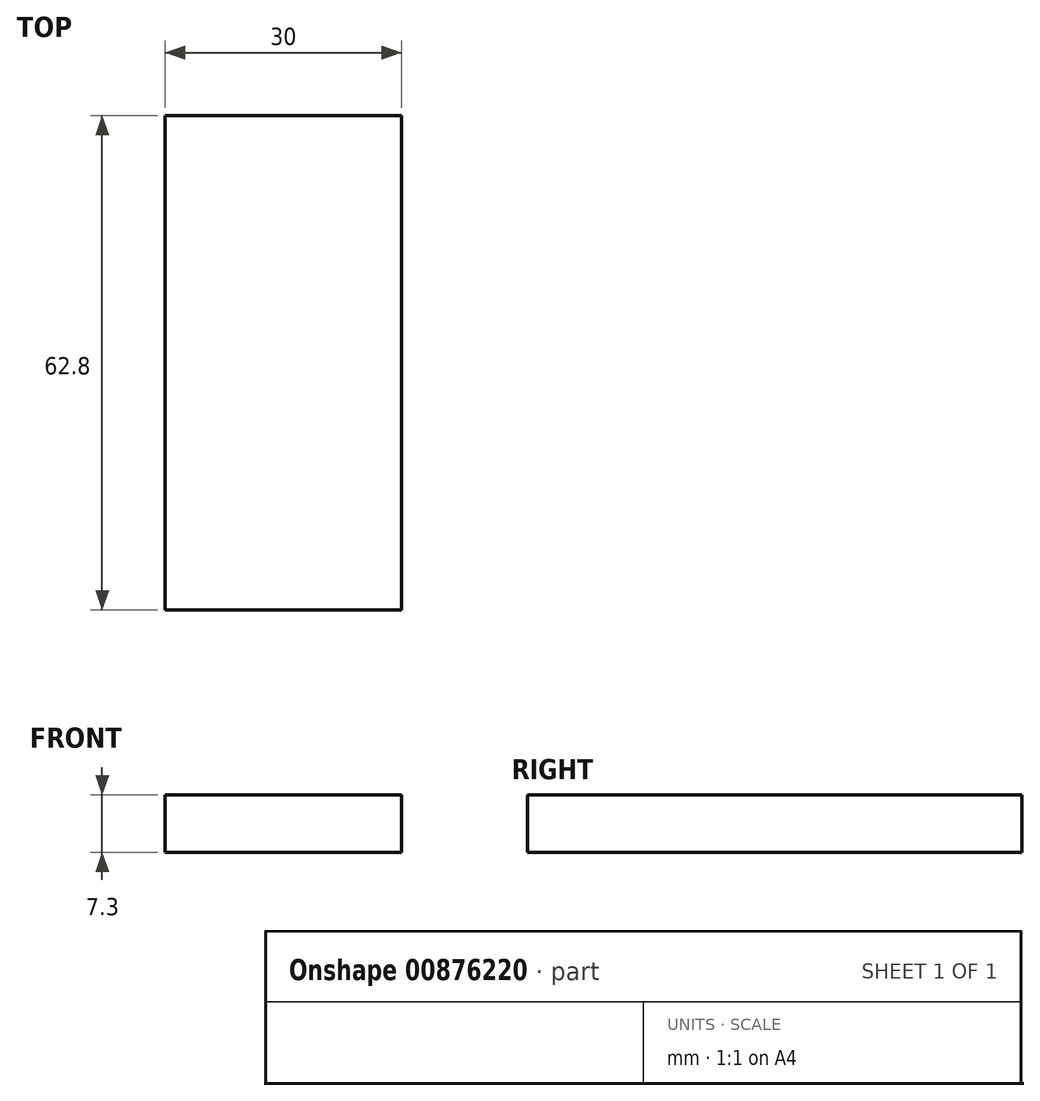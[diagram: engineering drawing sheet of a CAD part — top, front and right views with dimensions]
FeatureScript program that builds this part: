
annotation { "Feature Type Name" : "Feature", "Feature Type Description" : "" }
export const myFeature = defineFeature(function(context is Context, id is Id, definition is map)
    precondition{}
    {
        {
            var Q0;
            Q0=qCreatedBy(makeId("Top.planeOp"),FACE);
            var sketch = newSketch(context, id + "F0", { "sketchPlane" : qUnion([Q0])});
            skLineSegment(sketch, "E0.bottom", {"start": v(-15, 31.4) * mm, "end": v(15, 31.4) * mm});
            skLineSegment(sketch, "E0.top", {"start": v(-15, -31.4) * mm, "end": v(15, -31.4) * mm});
            skLineSegment(sketch, "E0.left", {"start": v(-15, 31.4) * mm, "end": v(-15, -31.4) * mm});
            skLineSegment(sketch, "E0.right", {"start": v(15, 31.4) * mm, "end": v(15, -31.4) * mm});
            skPoint(sketch, "E0.middle", {"position": v(0, 0) * mm});
            skSolve(sketch);
        }
        {
            var Q0;
            Q0=makeQuery(id+"F0.imprint","IMPRINT",FACE,{"disambiguationData":[TD([[makeQuery(id+"F0.imprint","IMPRINT",EDGE,{"derivedFrom":sQuery(id+"F0.wireOp",EDGE,"E0.bottom")}),-1.0]])]});
            extrude(context, id + "F1", {"entities" : qUnion([Q0]), "depth" : 7.3 * mm});
        }
    });
